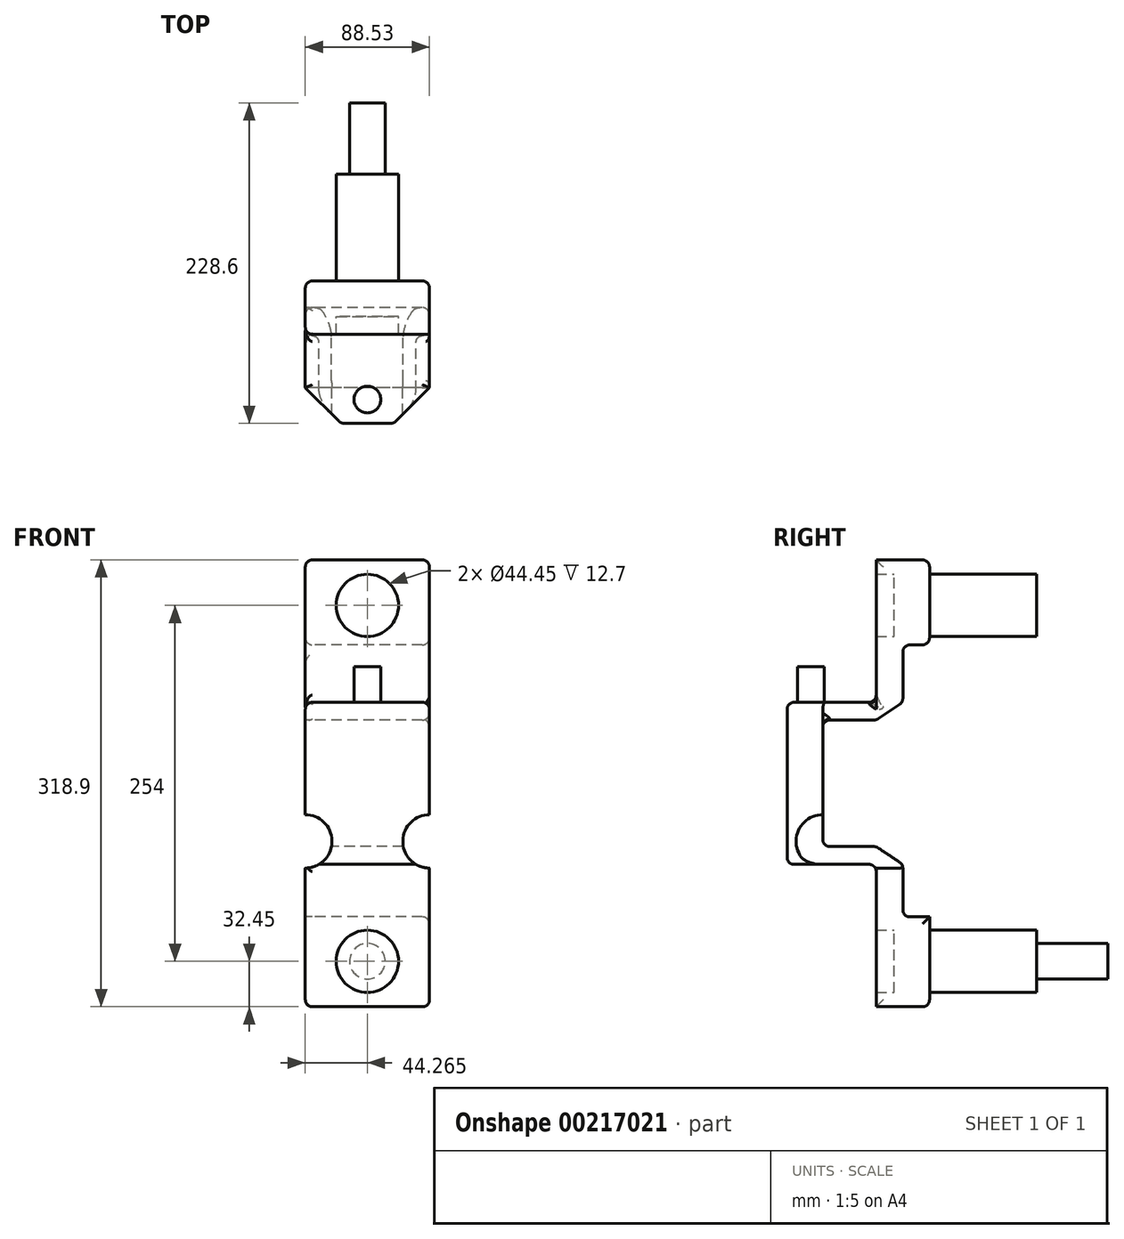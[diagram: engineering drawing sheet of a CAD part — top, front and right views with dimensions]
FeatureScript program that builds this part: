
annotation { "Feature Type Name" : "Feature", "Feature Type Description" : "" }
export const myFeature = defineFeature(function(context is Context, id is Id, definition is map)
    precondition{}
    {
        {
            var Q0;
            Q0=qCreatedBy(makeId("Front.planeOp"),FACE);
            var sketch = newSketch(context, id + "F0", { "sketchPlane" : qUnion([Q0])});
            skPoint(sketch, "E0.middle", {"position": v(-200.62, 122.45) * mm});
            skCircle(sketch, "E1", {"center": v(-200.62, 122.45) * mm, "radius": 22.23 * mm});
            skCircle(sketch, "E2", {"center": v(-200.62, -131.55) * mm, "radius": 22.23 * mm});
            skLineSegment(sketch, "E3", {"start": v(-200.62, 122.45) * mm, "end": v(-200.62, -131.55) * mm, "construction": true});
            skLineSegment(sketch, "E4.bottom", {"start": v(-156.36, -164) * mm, "end": v(-244.9, -164) * mm});
            skLineSegment(sketch, "E4.top", {"start": v(-156.36, 154.9) * mm, "end": v(-244.9, 154.9) * mm});
            skLineSegment(sketch, "E4.left", {"start": v(-156.36, -164) * mm, "end": v(-156.36, 154.9) * mm});
            skLineSegment(sketch, "E4.right", {"start": v(-244.9, -164) * mm, "end": v(-244.9, 154.9) * mm});
            skPoint(sketch, "E4.middle", {"position": v(-200.62, -4.55) * mm});
            skSolve(sketch);
        }
        {
            var Q0;
            Q0 = qSketchRegion(id + "F0", true);
            extrude(context, id + "F1", {"entities" : qUnion([Q0]), "depth" : 76.2 * mm});
        }
        {
            var Q0;
            Q0=makeQuery(id+"F1.opExtrude","SWEPT_FACE",FACE,{"disambiguationData":[OSD([sQuery(id+"F0.wireOp",EDGE,"E4.right")])]});
            var sketch = newSketch(context, id + "F2", { "sketchPlane" : qUnion([Q0])});
            skLineSegment(sketch, "E5", {"start": v(76.2, 154.9) * mm, "end": v(76.2, 53.3) * mm, "construction": true});
            skLineSegment(sketch, "E6", {"start": v(76.2, -164) * mm, "end": v(50.8, -164) * mm, "construction": true});
            skLineSegment(sketch, "E7", {"start": v(76.2, -164) * mm, "end": v(76.2, -62.4) * mm, "construction": true});
            skLineSegment(sketch, "E8", {"start": v(76.2, 154.9) * mm, "end": v(50.8, 154.9) * mm, "construction": true});
            skLineSegment(sketch, "E9", {"start": v(38.1, 154.9) * mm, "end": v(76.2, 53.3) * mm});
            skLineSegment(sketch, "E10", {"start": v(76.2, -62.4) * mm, "end": v(38.1, -164) * mm});
            skSolve(sketch);
        }
        {
            var Q0;
            {var subQ0=sQuery(id+"F2.wireOp",EDGE,"E10");Q0=makeQuery(id+"F2.imprint","IMPRINT",FACE,{"disambiguationData":[TD([[makeQuery(id+"F2.imprint","IMPRINT",EDGE,{"derivedFrom":subQ0}),1.0]])]});}
            var Q1;
            {var subQ0=sQuery(id+"F2.wireOp",EDGE,"E9");Q1=makeQuery(id+"F2.imprint","IMPRINT",FACE,{"disambiguationData":[TD([[makeQuery(id+"F2.imprint","IMPRINT",EDGE,{"derivedFrom":subQ0}),1.0]])]});}
            extrude(context, id + "F3", {"entities" : qUnion([Q0, Q1]), "operationType" : NewBodyOperationType.REMOVE, "endBound" : BoundingType.THROUGH_ALL, "oppositeDirection" : true, "depth" : 25.4 * mm});
        }
        {
            var Q0;
            Q0=makeQuery(id+"F0.imprint","IMPRINT",FACE,{"disambiguationData":[TD([[makeQuery(id+"F0.imprint","IMPRINT",EDGE,{"derivedFrom":sQuery(id+"F0.wireOp",EDGE,"E1")}),1.0]])]});
            var Q1;
            Q1=makeQuery(id+"F0.imprint","IMPRINT",FACE,{"disambiguationData":[TD([[makeQuery(id+"F0.imprint","IMPRINT",EDGE,{"derivedFrom":sQuery(id+"F0.wireOp",EDGE,"E2")}),1.0]])]});
            extrude(context, id + "F4", {"entities" : qUnion([Q0, Q1]), "operationType" : NewBodyOperationType.ADD, "depth" : 25.4 * mm, "hasSecondDirection" : true, "secondDirectionOppositeDirection" : true, "secondDirectionDepth" : 76.2 * mm});
        }
        {
            var Q0;
            Q0=makeQuery(id+"F1.opExtrude","SWEPT_FACE",FACE,{"disambiguationData":[OSD([sQuery(id+"F0.wireOp",EDGE,"E4.left")])]});
            var sketch = newSketch(context, id + "F5", { "sketchPlane" : qUnion([Q0])});
            skLineSegment(sketch, "E11", {"start": v(-38.1, 154.9) * mm, "end": v(-38.1, 53.3) * mm});
            skLineSegment(sketch, "E12", {"start": v(-38.1, 53.3) * mm, "end": v(-76.2, 53.3) * mm});
            skLineSegment(sketch, "E13", {"start": v(-76.2, -62.4) * mm, "end": v(-38.1, -62.4) * mm});
            skLineSegment(sketch, "E14", {"start": v(-38.1, -62.4) * mm, "end": v(-38.1, -164) * mm});
            skSolve(sketch);
        }
        {
            var Q0;
            Q0=makeQuery(id+"F5.imprint","IMPRINT",FACE,{"disambiguationData":[TD([[makeQuery(id+"F5.imprint","IMPRINT",EDGE,{"derivedFrom":sQuery(id+"F5.wireOp",EDGE,"E13")}),-1.0]])]});
            var Q1;
            Q1=makeQuery(id+"F5.imprint","IMPRINT",FACE,{"disambiguationData":[TD([[makeQuery(id+"F5.imprint","IMPRINT",EDGE,{"derivedFrom":sQuery(id+"F5.wireOp",EDGE,"E11")}),-1.0]])]});
            extrude(context, id + "F6", {"entities" : qUnion([Q0, Q1]), "operationType" : NewBodyOperationType.REMOVE, "endBound" : BoundingType.THROUGH_ALL, "oppositeDirection" : true, "depth" : 25.4 * mm});
        }
        {
            var Q0;
            Q0=makeQuery(id+"F4.opExtrude","CAP_FACE",FACE,{"disambiguationData":[OSD([sQuery(id+"F0.wireOp",EDGE,"E2")])],"isStart":true});
            extrude(context, id + "F7", {"entities" : qUnion([Q0]), "operationType" : NewBodyOperationType.ADD, "depth" : 50.8 * mm});
        }
        {
            var Q0;
            Q0=makeQuery(id+"F7.opExtrude","CAP_FACE",FACE,{"disambiguationData":[OSD([sQuery(id+"F0.wireOp",EDGE,"E2")])],"isStart":false});
            var sketch = newSketch(context, id + "F8", { "sketchPlane" : qUnion([Q0])});
            skCircle(sketch, "E15", {"center": v(200.62, -131.55) * mm, "radius": 12.7 * mm});
            skSolve(sketch);
        }
        {
            var Q0;
            Q0=makeQuery(id+"F8.imprint","IMPRINT",FACE,{"disambiguationData":[TD([[makeQuery(id+"F8.imprint","IMPRINT",EDGE,{"derivedFrom":sQuery(id+"F8.wireOp",EDGE,"E15")}),-1.0]])]});
            extrude(context, id + "F9", {"entities" : qUnion([Q0]), "operationType" : NewBodyOperationType.REMOVE, "oppositeDirection" : true, "depth" : 50.8 * mm});
        }
        {
            var Q0;
            Q0=makeQuery(id+"F1.opExtrude","CAP_FACE",FACE,{"disambiguationData":[OSD([sQuery(id+"F0.wireOp",EDGE,"E1"),sQuery(id+"F0.wireOp",EDGE,"E2"),sQuery(id+"F0.wireOp",EDGE,"E4.bottom"),sQuery(id+"F0.wireOp",EDGE,"E4.top"),sQuery(id+"F0.wireOp",EDGE,"E4.left"),sQuery(id+"F0.wireOp",EDGE,"E4.right")])],"isStart":false});
            extrude(context, id + "F10", {"entities" : qUnion([Q0]), "operationType" : NewBodyOperationType.ADD, "depth" : 25.4 * mm});
        }
        {
            var Q0;
            {var subQ0=sQuery(id+"F5.wireOp",EDGE,"E12");Q0=makeQuery(id+"F10.boolean.opBoolean","MERGE",FACE,{"derivedFrom":[makeQuery(id+"F6.boolean.opBoolean","COPY",FACE,{"derivedFrom":makeQuery(id+"F6.opExtrude","SWEPT_FACE",FACE,{"disambiguationData":[OSD([subQ0])]})}),makeQuery(id+"F10.opExtrude","SWEPT_FACE",FACE,{"disambiguationData":[OSD([sQuery(id+"F0.wireOp",EDGE,"E4.left"),sQuery(id+"F0.wireOp",EDGE,"E4.right"),sQuery(id+"F2.wireOp",EDGE,"E9"),subQ0])]})]});}
            var sketch = newSketch(context, id + "F11", { "sketchPlane" : qUnion([Q0])});
            skCircle(sketch, "E16", {"center": v(-200.62, -84.67) * mm, "radius": 9.53 * mm});
            skPoint(sketch, "E16.centerSnap0", {"position": v(-200.62, -101.6) * mm});
            skSolve(sketch);
        }
        {
            var Q0;
            Q0=makeQuery(id+"F11.imprint","IMPRINT",FACE,{"disambiguationData":[TD([[makeQuery(id+"F11.imprint","IMPRINT",EDGE,{"derivedFrom":sQuery(id+"F11.wireOp",EDGE,"E16")}),1.0]])]});
            extrude(context, id + "F12", {"entities" : qUnion([Q0]), "operationType" : NewBodyOperationType.ADD, "depth" : 25.4 * mm});
        }
        {
            var Q0;
            Q0=makeQuery(id+"F10.opExtrude","CAP_EDGE",EDGE,{"disambiguationData":[OSD([sQuery(id+"F0.wireOp",EDGE,"E4.right")])],"isStart":false});
            var Q1;
            Q1=makeQuery(id+"F10.opExtrude","CAP_EDGE",EDGE,{"disambiguationData":[OSD([sQuery(id+"F0.wireOp",EDGE,"E4.left")])],"isStart":false});
            chamfer(context, id + "F13", {"entities" : qUnion([Q0, Q1]), "width" : 25.4 * mm, "tangentPropagation" : true});
        }
        {
            var Q0;
            {var subQ0=sQuery(id+"F0.wireOp",EDGE,"E4.right");Q0=makeQuery(id+"F10.boolean.opBoolean","MERGE",FACE,{"derivedFrom":[makeQuery(id+"F1.opExtrude","SWEPT_FACE",FACE,{"disambiguationData":[OSD([subQ0])]}),makeQuery(id+"F10.opExtrude","SWEPT_FACE",FACE,{"disambiguationData":[OSD([subQ0])]})]});}
            var sketch = newSketch(context, id + "F14", { "sketchPlane" : qUnion([Q0])});
            skLineSegment(sketch, "E17", {"start": v(0, 94.28) * mm, "end": v(19.05, 94.28) * mm});
            skLineSegment(sketch, "E18", {"start": v(19.05, 94.28) * mm, "end": v(19.05, 53.3) * mm});
            skLineSegment(sketch, "E19", {"start": v(19.05, -99.86) * mm, "end": v(0, -99.86) * mm});
            skLineSegment(sketch, "E20.0", {"start": v(76.2, 40.6) * mm, "end": v(38.1, 40.6) * mm});
            skLineSegment(sketch, "E21.0", {"start": v(38.1, -49.7) * mm, "end": v(76.2, -49.7) * mm});
            skLineSegment(sketch, "E22", {"start": v(38.1, 40.6) * mm, "end": v(19.05, 53.3) * mm});
            skLineSegment(sketch, "E23", {"start": v(38.1, -49.7) * mm, "end": v(19.05, -62.4) * mm});
            skLineSegment(sketch, "E24.trimOffspring", {"start": v(19.05, -62.4) * mm, "end": v(19.05, -99.86) * mm});
            skSolve(sketch);
        }
        {
            var Q0;
            {var subQ2=sQuery(id+"F14.wireOp",EDGE,"E17");Q0=makeQuery(id+"F14.imprint","IMPRINT",FACE,{"disambiguationData":[TD([[makeQuery(id+"F14.imprint","IMPRINT",EDGE,{"derivedFrom":subQ2}),-1.0]])]});}
            extrude(context, id + "F15", {"entities" : qUnion([Q0]), "operationType" : NewBodyOperationType.REMOVE, "endBound" : BoundingType.THROUGH_ALL, "oppositeDirection" : true, "depth" : 25.4 * mm});
        }
        {
            var Q0;
            {var subQ0=sQuery(id+"F5.wireOp",EDGE,"E13");var subQ1=sQuery(id+"F0.wireOp",EDGE,"E4.left");Q0=makeQuery(id+"F13.opChamfer","BLEND_EDGE",EDGE,{"blendedFrom":[makeQuery(id+"F10.opExtrude","CAP_EDGE",EDGE,{"disambiguationData":[OSD([subQ1])],"isStart":false}),makeQuery(id+"F10.boolean.opBoolean","MERGE",FACE,{"derivedFrom":[makeQuery(id+"F6.boolean.opBoolean","COPY",FACE,{"derivedFrom":makeQuery(id+"F6.opExtrude","SWEPT_FACE",FACE,{"disambiguationData":[OSD([subQ0])]})}),makeQuery(id+"F10.opExtrude","SWEPT_FACE",FACE,{"disambiguationData":[OSD([subQ1,sQuery(id+"F0.wireOp",EDGE,"E4.right"),sQuery(id+"F2.wireOp",EDGE,"E10"),subQ0])]})]})],"blendedInto":[makeQuery(id+"F10.boolean.opBoolean","MERGE",FACE,{"derivedFrom":[makeQuery(id+"F6.boolean.opBoolean","COPY",FACE,{"derivedFrom":makeQuery(id+"F6.opExtrude","SWEPT_FACE",FACE,{"disambiguationData":[OSD([subQ0])]})}),makeQuery(id+"F10.opExtrude","SWEPT_FACE",FACE,{"disambiguationData":[OSD([subQ1,sQuery(id+"F0.wireOp",EDGE,"E4.right"),sQuery(id+"F2.wireOp",EDGE,"E10"),subQ0])]})]})]});}
            var Q1;
            Q1=makeQuery(id+"F10.opExtrude","CAP_EDGE",EDGE,{"disambiguationData":[OSD([sQuery(id+"F0.wireOp",EDGE,"E4.left"),sQuery(id+"F0.wireOp",EDGE,"E4.right"),sQuery(id+"F2.wireOp",EDGE,"E10"),sQuery(id+"F5.wireOp",EDGE,"E13")])],"isStart":false});
            var Q2;
            {var subQ0=sQuery(id+"F5.wireOp",EDGE,"E13");var subQ1=sQuery(id+"F0.wireOp",EDGE,"E4.right");Q2=makeQuery(id+"F13.opChamfer","BLEND_EDGE",EDGE,{"blendedFrom":[makeQuery(id+"F10.opExtrude","CAP_EDGE",EDGE,{"disambiguationData":[OSD([subQ1])],"isStart":false}),makeQuery(id+"F10.boolean.opBoolean","MERGE",FACE,{"derivedFrom":[makeQuery(id+"F6.boolean.opBoolean","COPY",FACE,{"derivedFrom":makeQuery(id+"F6.opExtrude","SWEPT_FACE",FACE,{"disambiguationData":[OSD([subQ0])]})}),makeQuery(id+"F10.opExtrude","SWEPT_FACE",FACE,{"disambiguationData":[OSD([sQuery(id+"F0.wireOp",EDGE,"E4.left"),subQ1,sQuery(id+"F2.wireOp",EDGE,"E10"),subQ0])]})]})],"blendedInto":[makeQuery(id+"F10.boolean.opBoolean","MERGE",FACE,{"derivedFrom":[makeQuery(id+"F6.boolean.opBoolean","COPY",FACE,{"derivedFrom":makeQuery(id+"F6.opExtrude","SWEPT_FACE",FACE,{"disambiguationData":[OSD([subQ0])]})}),makeQuery(id+"F10.opExtrude","SWEPT_FACE",FACE,{"disambiguationData":[OSD([sQuery(id+"F0.wireOp",EDGE,"E4.left"),subQ1,sQuery(id+"F2.wireOp",EDGE,"E10"),subQ0])]})]})]});}
            var Q3;
            {var subQ0=sQuery(id+"F0.wireOp",EDGE,"E4.right");Q3=makeQuery(id+"F10.boolean.opBoolean","MERGE",EDGE,{"derivedFrom":[makeQuery(id+"F6.boolean.opBoolean","INTERSECT",EDGE,{"derivedFrom":[makeQuery(id+"F1.opExtrude","SWEPT_FACE",FACE,{"disambiguationData":[OSD([subQ0])]}),makeQuery(id+"F6.opExtrude","SWEPT_FACE",FACE,{"disambiguationData":[OSD([sQuery(id+"F5.wireOp",EDGE,"E13")])]})]}),makeQuery(id+"F10.opExtrude","SWEPT_EDGE",EDGE,{"disambiguationData":[OSD([subQ0,sQuery(id+"F2.wireOp",EDGE,"E10")])]})]});}
            var Q4;
            Q4=makeQuery(id+"F6.boolean.opBoolean","INTERSECT",EDGE,{"derivedFrom":[makeQuery(id+"F1.opExtrude","SWEPT_FACE",FACE,{"disambiguationData":[OSD([sQuery(id+"F0.wireOp",EDGE,"E4.right")])]}),makeQuery(id+"F6.opExtrude","SWEPT_FACE",FACE,{"disambiguationData":[OSD([sQuery(id+"F5.wireOp",EDGE,"E14")])]})]});
            var Q5;
            {var subQ0=sQuery(id+"F2.wireOp",EDGE,"E10");var subQ1=sQuery(id+"F0.wireOp",EDGE,"E4.bottom");Q5=makeQuery(id+"F6.boolean.opBoolean","MERGE",EDGE,{"derivedFrom":[makeQuery(id+"F3.boolean.opBoolean","COPY",EDGE,{"derivedFrom":makeQuery(id+"F3.opExtrude","SWEPT_EDGE",EDGE,{"disambiguationData":[OSD([subQ1,sQuery(id+"F0.wireOp",EDGE,"E4.right"),subQ0])]})}),makeQuery(id+"F6.opExtrude","SWEPT_EDGE",EDGE,{"disambiguationData":[OSD([subQ1,sQuery(id+"F0.wireOp",EDGE,"E4.left"),subQ0,sQuery(id+"F5.wireOp",EDGE,"E14")])]})]});}
            var Q6;
            Q6=makeQuery(id+"F6.boolean.opBoolean","COPY",EDGE,{"derivedFrom":makeQuery(id+"F6.opExtrude","CAP_EDGE",EDGE,{"disambiguationData":[OSD([sQuery(id+"F5.wireOp",EDGE,"E14")])],"isStart":true})});
            var Q7;
            {var subQ0=sQuery(id+"F5.wireOp",EDGE,"E13");Q7=makeQuery(id+"F10.boolean.opBoolean","MERGE",EDGE,{"derivedFrom":[makeQuery(id+"F6.boolean.opBoolean","COPY",EDGE,{"derivedFrom":makeQuery(id+"F6.opExtrude","CAP_EDGE",EDGE,{"disambiguationData":[OSD([subQ0])],"isStart":true})}),makeQuery(id+"F10.opExtrude","SWEPT_EDGE",EDGE,{"disambiguationData":[OSD([sQuery(id+"F0.wireOp",EDGE,"E4.left"),sQuery(id+"F2.wireOp",EDGE,"E10"),subQ0])]})]});}
            var Q8;
            {var subQ0=sQuery(id+"F0.wireOp",EDGE,"E4.left");Q8=makeQuery(id+"F13.opChamfer","BLEND_EDGE",EDGE,{"blendedFrom":[makeQuery(id+"F10.opExtrude","CAP_EDGE",EDGE,{"disambiguationData":[OSD([subQ0])],"isStart":false}),makeQuery(id+"F10.opExtrude","CAP_FACE",FACE,{"disambiguationData":[OSD([sQuery(id+"F0.wireOp",EDGE,"E1"),sQuery(id+"F0.wireOp",EDGE,"E2"),sQuery(id+"F0.wireOp",EDGE,"E4.bottom"),sQuery(id+"F0.wireOp",EDGE,"E4.top"),subQ0,sQuery(id+"F0.wireOp",EDGE,"E4.right")])],"isStart":false})],"blendedInto":[makeQuery(id+"F10.opExtrude","CAP_FACE",FACE,{"disambiguationData":[OSD([sQuery(id+"F0.wireOp",EDGE,"E1"),sQuery(id+"F0.wireOp",EDGE,"E2"),sQuery(id+"F0.wireOp",EDGE,"E4.bottom"),sQuery(id+"F0.wireOp",EDGE,"E4.top"),subQ0,sQuery(id+"F0.wireOp",EDGE,"E4.right")])],"isStart":false})]});}
            var Q9;
            {var subQ0=sQuery(id+"F0.wireOp",EDGE,"E4.right");Q9=makeQuery(id+"F13.opChamfer","BLEND_EDGE",EDGE,{"blendedFrom":[makeQuery(id+"F10.opExtrude","CAP_EDGE",EDGE,{"disambiguationData":[OSD([subQ0])],"isStart":false}),makeQuery(id+"F10.opExtrude","CAP_FACE",FACE,{"disambiguationData":[OSD([sQuery(id+"F0.wireOp",EDGE,"E1"),sQuery(id+"F0.wireOp",EDGE,"E2"),sQuery(id+"F0.wireOp",EDGE,"E4.bottom"),sQuery(id+"F0.wireOp",EDGE,"E4.top"),sQuery(id+"F0.wireOp",EDGE,"E4.left"),subQ0])],"isStart":false})],"blendedInto":[makeQuery(id+"F10.opExtrude","CAP_FACE",FACE,{"disambiguationData":[OSD([sQuery(id+"F0.wireOp",EDGE,"E1"),sQuery(id+"F0.wireOp",EDGE,"E2"),sQuery(id+"F0.wireOp",EDGE,"E4.bottom"),sQuery(id+"F0.wireOp",EDGE,"E4.top"),sQuery(id+"F0.wireOp",EDGE,"E4.left"),subQ0])],"isStart":false})]});}
            var Q10;
            {var subQ0=sQuery(id+"F5.wireOp",EDGE,"E12");var subQ1=sQuery(id+"F0.wireOp",EDGE,"E4.left");Q10=makeQuery(id+"F13.opChamfer","BLEND_EDGE",EDGE,{"blendedFrom":[makeQuery(id+"F10.opExtrude","CAP_EDGE",EDGE,{"disambiguationData":[OSD([subQ1])],"isStart":false}),makeQuery(id+"F10.boolean.opBoolean","MERGE",FACE,{"derivedFrom":[makeQuery(id+"F6.boolean.opBoolean","COPY",FACE,{"derivedFrom":makeQuery(id+"F6.opExtrude","SWEPT_FACE",FACE,{"disambiguationData":[OSD([subQ0])]})}),makeQuery(id+"F10.opExtrude","SWEPT_FACE",FACE,{"disambiguationData":[OSD([subQ1,sQuery(id+"F0.wireOp",EDGE,"E4.right"),sQuery(id+"F2.wireOp",EDGE,"E9"),subQ0])]})]})],"blendedInto":[makeQuery(id+"F10.boolean.opBoolean","MERGE",FACE,{"derivedFrom":[makeQuery(id+"F6.boolean.opBoolean","COPY",FACE,{"derivedFrom":makeQuery(id+"F6.opExtrude","SWEPT_FACE",FACE,{"disambiguationData":[OSD([subQ0])]})}),makeQuery(id+"F10.opExtrude","SWEPT_FACE",FACE,{"disambiguationData":[OSD([subQ1,sQuery(id+"F0.wireOp",EDGE,"E4.right"),sQuery(id+"F2.wireOp",EDGE,"E9"),subQ0])]})]})]});}
            var Q11;
            Q11=makeQuery(id+"F10.opExtrude","CAP_EDGE",EDGE,{"disambiguationData":[OSD([sQuery(id+"F0.wireOp",EDGE,"E4.left"),sQuery(id+"F0.wireOp",EDGE,"E4.right"),sQuery(id+"F2.wireOp",EDGE,"E9"),sQuery(id+"F5.wireOp",EDGE,"E12")])],"isStart":false});
            var Q12;
            {var subQ0=sQuery(id+"F5.wireOp",EDGE,"E12");var subQ1=sQuery(id+"F0.wireOp",EDGE,"E4.right");Q12=makeQuery(id+"F13.opChamfer","BLEND_EDGE",EDGE,{"blendedFrom":[makeQuery(id+"F10.opExtrude","CAP_EDGE",EDGE,{"disambiguationData":[OSD([subQ1])],"isStart":false}),makeQuery(id+"F10.boolean.opBoolean","MERGE",FACE,{"derivedFrom":[makeQuery(id+"F6.boolean.opBoolean","COPY",FACE,{"derivedFrom":makeQuery(id+"F6.opExtrude","SWEPT_FACE",FACE,{"disambiguationData":[OSD([subQ0])]})}),makeQuery(id+"F10.opExtrude","SWEPT_FACE",FACE,{"disambiguationData":[OSD([sQuery(id+"F0.wireOp",EDGE,"E4.left"),subQ1,sQuery(id+"F2.wireOp",EDGE,"E9"),subQ0])]})]})],"blendedInto":[makeQuery(id+"F10.boolean.opBoolean","MERGE",FACE,{"derivedFrom":[makeQuery(id+"F6.boolean.opBoolean","COPY",FACE,{"derivedFrom":makeQuery(id+"F6.opExtrude","SWEPT_FACE",FACE,{"disambiguationData":[OSD([subQ0])]})}),makeQuery(id+"F10.opExtrude","SWEPT_FACE",FACE,{"disambiguationData":[OSD([sQuery(id+"F0.wireOp",EDGE,"E4.left"),subQ1,sQuery(id+"F2.wireOp",EDGE,"E9"),subQ0])]})]})]});}
            var Q13;
            Q13=makeQuery(id+"F6.boolean.opBoolean","INTERSECT",EDGE,{"derivedFrom":[makeQuery(id+"F1.opExtrude","SWEPT_FACE",FACE,{"disambiguationData":[OSD([sQuery(id+"F0.wireOp",EDGE,"E4.right")])]}),makeQuery(id+"F6.opExtrude","SWEPT_FACE",FACE,{"disambiguationData":[OSD([sQuery(id+"F5.wireOp",EDGE,"E11")])]})]});
            var Q14;
            {var subQ0=sQuery(id+"F2.wireOp",EDGE,"E9");var subQ1=sQuery(id+"F0.wireOp",EDGE,"E4.top");Q14=makeQuery(id+"F6.boolean.opBoolean","MERGE",EDGE,{"derivedFrom":[makeQuery(id+"F3.boolean.opBoolean","COPY",EDGE,{"derivedFrom":makeQuery(id+"F3.opExtrude","SWEPT_EDGE",EDGE,{"disambiguationData":[OSD([subQ1,sQuery(id+"F0.wireOp",EDGE,"E4.right"),subQ0])]})}),makeQuery(id+"F6.opExtrude","SWEPT_EDGE",EDGE,{"disambiguationData":[OSD([subQ1,sQuery(id+"F0.wireOp",EDGE,"E4.left"),subQ0,sQuery(id+"F5.wireOp",EDGE,"E11")])]})]});}
            var Q15;
            Q15=makeQuery(id+"F6.boolean.opBoolean","COPY",EDGE,{"derivedFrom":makeQuery(id+"F6.opExtrude","CAP_EDGE",EDGE,{"disambiguationData":[OSD([sQuery(id+"F5.wireOp",EDGE,"E11")])],"isStart":true})});
            var Q16;
            Q16=makeQuery(id+"F1.opExtrude","SWEPT_EDGE",EDGE,{"disambiguationData":[OSD([sQuery(id+"F0.wireOp",EDGE,"E4.top"),sQuery(id+"F0.wireOp",EDGE,"E4.left")])]});
            var Q17;
            {var subQ0=sQuery(id+"F0.wireOp",EDGE,"E4.left");var subQ1=sQuery(id+"F0.wireOp",EDGE,"E4.top");Q17=makeQuery(id+"F15.boolean.opBoolean","SPLIT",EDGE,{"disambiguationData":[TD([makeQuery(id+"F1.opExtrude","SWEPT_FACE",FACE,{"disambiguationData":[OSD([subQ1])]})])],"derivedFrom":makeQuery(id+"F1.opExtrude","CAP_EDGE",EDGE,{"disambiguationData":[OSD([subQ0])],"isStart":true})});}
            var Q18;
            {var subQ0=sQuery(id+"F0.wireOp",EDGE,"E4.left");Q18=makeQuery(id+"F15.boolean.opBoolean","INTERSECT",EDGE,{"derivedFrom":[makeQuery(id+"F10.boolean.opBoolean","MERGE",FACE,{"derivedFrom":[makeQuery(id+"F1.opExtrude","SWEPT_FACE",FACE,{"disambiguationData":[OSD([subQ0])]}),makeQuery(id+"F10.opExtrude","SWEPT_FACE",FACE,{"disambiguationData":[OSD([subQ0])]})]}),makeQuery(id+"F15.opExtrude","SWEPT_FACE",FACE,{"disambiguationData":[OSD([sQuery(id+"F14.wireOp",EDGE,"E21.0")])]})]});}
            var Q19;
            {var subQ0=sQuery(id+"F0.wireOp",EDGE,"E4.left");Q19=makeQuery(id+"F15.boolean.opBoolean","INTERSECT",EDGE,{"derivedFrom":[makeQuery(id+"F10.boolean.opBoolean","MERGE",FACE,{"derivedFrom":[makeQuery(id+"F1.opExtrude","SWEPT_FACE",FACE,{"disambiguationData":[OSD([subQ0])]}),makeQuery(id+"F10.opExtrude","SWEPT_FACE",FACE,{"disambiguationData":[OSD([subQ0])]})]}),makeQuery(id+"F15.opExtrude","SWEPT_FACE",FACE,{"disambiguationData":[OSD([sQuery(id+"F14.wireOp",EDGE,"E23")])]})]});}
            var Q20;
            {var subQ0=sQuery(id+"F0.wireOp",EDGE,"E4.left");Q20=makeQuery(id+"F15.boolean.opBoolean","INTERSECT",EDGE,{"derivedFrom":[makeQuery(id+"F10.boolean.opBoolean","MERGE",FACE,{"derivedFrom":[makeQuery(id+"F1.opExtrude","SWEPT_FACE",FACE,{"disambiguationData":[OSD([subQ0])]}),makeQuery(id+"F10.opExtrude","SWEPT_FACE",FACE,{"disambiguationData":[OSD([subQ0])]})]}),makeQuery(id+"F15.opExtrude","SWEPT_FACE",FACE,{"disambiguationData":[OSD([sQuery(id+"F14.wireOp",EDGE,"E24.trimOffspring")])]})]});}
            var Q21;
            {var subQ0=sQuery(id+"F0.wireOp",EDGE,"E4.left");Q21=makeQuery(id+"F15.boolean.opBoolean","INTERSECT",EDGE,{"derivedFrom":[makeQuery(id+"F10.boolean.opBoolean","MERGE",FACE,{"derivedFrom":[makeQuery(id+"F1.opExtrude","SWEPT_FACE",FACE,{"disambiguationData":[OSD([subQ0])]}),makeQuery(id+"F10.opExtrude","SWEPT_FACE",FACE,{"disambiguationData":[OSD([subQ0])]})]}),makeQuery(id+"F15.opExtrude","SWEPT_FACE",FACE,{"disambiguationData":[OSD([sQuery(id+"F14.wireOp",EDGE,"E19")])]})]});}
            var Q22;
            {var subQ0=sQuery(id+"F0.wireOp",EDGE,"E4.left");var subQ1=sQuery(id+"F0.wireOp",EDGE,"E4.bottom");Q22=makeQuery(id+"F15.boolean.opBoolean","SPLIT",EDGE,{"disambiguationData":[TD([makeQuery(id+"F1.opExtrude","SWEPT_FACE",FACE,{"disambiguationData":[OSD([subQ1])]})])],"derivedFrom":makeQuery(id+"F1.opExtrude","CAP_EDGE",EDGE,{"disambiguationData":[OSD([subQ0])],"isStart":true})});}
            var Q23;
            Q23=makeQuery(id+"F1.opExtrude","SWEPT_EDGE",EDGE,{"disambiguationData":[OSD([sQuery(id+"F0.wireOp",EDGE,"E4.bottom"),sQuery(id+"F0.wireOp",EDGE,"E4.left")])]});
            var Q24;
            Q24=makeQuery(id+"F1.opExtrude","CAP_EDGE",EDGE,{"disambiguationData":[OSD([sQuery(id+"F0.wireOp",EDGE,"E4.bottom")])],"isStart":true});
            var Q25;
            Q25=makeQuery(id+"F1.opExtrude","SWEPT_EDGE",EDGE,{"disambiguationData":[OSD([sQuery(id+"F0.wireOp",EDGE,"E4.bottom"),sQuery(id+"F0.wireOp",EDGE,"E4.right")])]});
            var Q26;
            {var subQ0=sQuery(id+"F0.wireOp",EDGE,"E4.right");var subQ1=sQuery(id+"F0.wireOp",EDGE,"E4.bottom");Q26=makeQuery(id+"F15.boolean.opBoolean","SPLIT",EDGE,{"disambiguationData":[TD([makeQuery(id+"F1.opExtrude","SWEPT_FACE",FACE,{"disambiguationData":[OSD([subQ1])]})])],"derivedFrom":makeQuery(id+"F1.opExtrude","CAP_EDGE",EDGE,{"disambiguationData":[OSD([subQ0])],"isStart":true})});}
            var Q27;
            Q27=makeQuery(id+"F15.boolean.opBoolean","COPY",EDGE,{"derivedFrom":makeQuery(id+"F15.opExtrude","CAP_EDGE",EDGE,{"disambiguationData":[OSD([sQuery(id+"F14.wireOp",EDGE,"E19")])],"isStart":true})});
            var Q28;
            Q28=makeQuery(id+"F15.boolean.opBoolean","COPY",EDGE,{"derivedFrom":makeQuery(id+"F15.opExtrude","CAP_EDGE",EDGE,{"disambiguationData":[OSD([sQuery(id+"F14.wireOp",EDGE,"E24.trimOffspring")])],"isStart":true})});
            var Q29;
            Q29=makeQuery(id+"F15.boolean.opBoolean","COPY",EDGE,{"derivedFrom":makeQuery(id+"F15.opExtrude","CAP_EDGE",EDGE,{"disambiguationData":[OSD([sQuery(id+"F14.wireOp",EDGE,"E23")])],"isStart":true})});
            var Q30;
            Q30=makeQuery(id+"F15.boolean.opBoolean","COPY",EDGE,{"derivedFrom":makeQuery(id+"F15.opExtrude","CAP_EDGE",EDGE,{"disambiguationData":[OSD([sQuery(id+"F14.wireOp",EDGE,"E21.0")])],"isStart":true})});
            var Q31;
            Q31=makeQuery(id+"F15.boolean.opBoolean","COPY",EDGE,{"derivedFrom":makeQuery(id+"F15.opExtrude","CAP_EDGE",EDGE,{"disambiguationData":[OSD([sQuery(id+"F14.wireOp",EDGE,"E20.0")])],"isStart":true})});
            var Q32;
            Q32=makeQuery(id+"F15.boolean.opBoolean","COPY",EDGE,{"derivedFrom":makeQuery(id+"F15.opExtrude","CAP_EDGE",EDGE,{"disambiguationData":[OSD([sQuery(id+"F14.wireOp",EDGE,"E22")])],"isStart":true})});
            var Q33;
            Q33=makeQuery(id+"F15.boolean.opBoolean","COPY",EDGE,{"derivedFrom":makeQuery(id+"F15.opExtrude","CAP_EDGE",EDGE,{"disambiguationData":[OSD([sQuery(id+"F14.wireOp",EDGE,"E18")])],"isStart":true})});
            var Q34;
            Q34=makeQuery(id+"F15.boolean.opBoolean","COPY",EDGE,{"derivedFrom":makeQuery(id+"F15.opExtrude","CAP_EDGE",EDGE,{"disambiguationData":[OSD([sQuery(id+"F14.wireOp",EDGE,"E17")])],"isStart":true})});
            var Q35;
            {var subQ0=sQuery(id+"F0.wireOp",EDGE,"E4.right");var subQ1=sQuery(id+"F0.wireOp",EDGE,"E4.top");Q35=makeQuery(id+"F15.boolean.opBoolean","SPLIT",EDGE,{"disambiguationData":[TD([makeQuery(id+"F1.opExtrude","SWEPT_FACE",FACE,{"disambiguationData":[OSD([subQ1])]})])],"derivedFrom":makeQuery(id+"F1.opExtrude","CAP_EDGE",EDGE,{"disambiguationData":[OSD([subQ0])],"isStart":true})});}
            var Q36;
            Q36=makeQuery(id+"F1.opExtrude","SWEPT_EDGE",EDGE,{"disambiguationData":[OSD([sQuery(id+"F0.wireOp",EDGE,"E4.top"),sQuery(id+"F0.wireOp",EDGE,"E4.right")])]});
            var Q37;
            Q37=makeQuery(id+"F1.opExtrude","CAP_EDGE",EDGE,{"disambiguationData":[OSD([sQuery(id+"F0.wireOp",EDGE,"E4.top")])],"isStart":true});
            var Q38;
            {var subQ0=sQuery(id+"F5.wireOp",EDGE,"E12");Q38=makeQuery(id+"F10.boolean.opBoolean","MERGE",EDGE,{"derivedFrom":[makeQuery(id+"F6.boolean.opBoolean","COPY",EDGE,{"derivedFrom":makeQuery(id+"F6.opExtrude","CAP_EDGE",EDGE,{"disambiguationData":[OSD([subQ0])],"isStart":true})}),makeQuery(id+"F10.opExtrude","SWEPT_EDGE",EDGE,{"disambiguationData":[OSD([sQuery(id+"F0.wireOp",EDGE,"E4.left"),sQuery(id+"F2.wireOp",EDGE,"E9"),subQ0])]})]});}
            var Q39;
            {var subQ0=sQuery(id+"F0.wireOp",EDGE,"E4.right");Q39=makeQuery(id+"F10.boolean.opBoolean","MERGE",EDGE,{"derivedFrom":[makeQuery(id+"F6.boolean.opBoolean","INTERSECT",EDGE,{"derivedFrom":[makeQuery(id+"F1.opExtrude","SWEPT_FACE",FACE,{"disambiguationData":[OSD([subQ0])]}),makeQuery(id+"F6.opExtrude","SWEPT_FACE",FACE,{"disambiguationData":[OSD([sQuery(id+"F5.wireOp",EDGE,"E12")])]})]}),makeQuery(id+"F10.opExtrude","SWEPT_EDGE",EDGE,{"disambiguationData":[OSD([subQ0,sQuery(id+"F2.wireOp",EDGE,"E9")])]})]});}
            var Q40;
            Q40=makeQuery(id+"F15.boolean.opBoolean","COPY",EDGE,{"derivedFrom":makeQuery(id+"F15.opExtrude","SWEPT_EDGE",EDGE,{"disambiguationData":[OSD([sQuery(id+"F0.wireOp",EDGE,"E4.right"),sQuery(id+"F14.wireOp",EDGE,"E19")])]})});
            var Q41;
            Q41=makeQuery(id+"F15.boolean.opBoolean","COPY",EDGE,{"derivedFrom":makeQuery(id+"F15.opExtrude","SWEPT_EDGE",EDGE,{"disambiguationData":[OSD([sQuery(id+"F14.wireOp",EDGE,"E19"),sQuery(id+"F14.wireOp",EDGE,"E24.trimOffspring")])]})});
            var Q42;
            Q42=makeQuery(id+"F15.boolean.opBoolean","COPY",EDGE,{"derivedFrom":makeQuery(id+"F15.opExtrude","SWEPT_EDGE",EDGE,{"disambiguationData":[OSD([sQuery(id+"F14.wireOp",EDGE,"E23"),sQuery(id+"F14.wireOp",EDGE,"E24.trimOffspring")])]})});
            var Q43;
            Q43=makeQuery(id+"F15.boolean.opBoolean","COPY",EDGE,{"derivedFrom":makeQuery(id+"F15.opExtrude","SWEPT_EDGE",EDGE,{"disambiguationData":[OSD([sQuery(id+"F14.wireOp",EDGE,"E21.0"),sQuery(id+"F14.wireOp",EDGE,"E23")])]})});
            fillet(context, id + "F16", {"entities" : qUnion([Q0, Q1, Q2, Q3, Q4, Q5, Q6, Q7, Q8, Q9, Q10, Q11, Q12, Q13, Q14, Q15, Q16, Q17, Q18, Q19, Q20, Q21, Q22, Q23, Q24, Q25, Q26, Q27, Q28, Q29, Q30, Q31, Q32, Q33, Q34, Q35, Q36, Q37, Q38, Q39, Q40, Q41, Q42, Q43]), "radius" : 5.08 * mm, "tangentPropagation" : true, "allowEdgeOverflow" : false});
        }
        {
            var Q0;
            {var subQ0=sQuery(id+"F0.wireOp",EDGE,"E4.left");Q0=makeQuery(id+"F15.boolean.opBoolean","INTERSECT",EDGE,{"derivedFrom":[makeQuery(id+"F10.boolean.opBoolean","MERGE",FACE,{"derivedFrom":[makeQuery(id+"F1.opExtrude","SWEPT_FACE",FACE,{"disambiguationData":[OSD([subQ0])]}),makeQuery(id+"F10.opExtrude","SWEPT_FACE",FACE,{"disambiguationData":[OSD([subQ0])]})]}),makeQuery(id+"F15.opExtrude","SWEPT_FACE",FACE,{"disambiguationData":[OSD([sQuery(id+"F14.wireOp",EDGE,"E20.0")])]})]});}
            var Q1;
            Q1=makeQuery(id+"F15.boolean.opBoolean","COPY",FACE,{"derivedFrom":makeQuery(id+"F15.opExtrude","SWEPT_FACE",FACE,{"disambiguationData":[OSD([sQuery(id+"F14.wireOp",EDGE,"E22")])]})});
            var Q2;
            {var subQ0=sQuery(id+"F0.wireOp",EDGE,"E4.left");Q2=makeQuery(id+"F15.boolean.opBoolean","INTERSECT",EDGE,{"derivedFrom":[makeQuery(id+"F10.boolean.opBoolean","MERGE",FACE,{"derivedFrom":[makeQuery(id+"F1.opExtrude","SWEPT_FACE",FACE,{"disambiguationData":[OSD([subQ0])]}),makeQuery(id+"F10.opExtrude","SWEPT_FACE",FACE,{"disambiguationData":[OSD([subQ0])]})]}),makeQuery(id+"F15.opExtrude","SWEPT_FACE",FACE,{"disambiguationData":[OSD([sQuery(id+"F14.wireOp",EDGE,"E17")])]})]});}
            var Q3;
            {var subQ0=sQuery(id+"F0.wireOp",EDGE,"E4.left");Q3=makeQuery(id+"F15.boolean.opBoolean","INTERSECT",EDGE,{"derivedFrom":[makeQuery(id+"F10.boolean.opBoolean","MERGE",FACE,{"derivedFrom":[makeQuery(id+"F1.opExtrude","SWEPT_FACE",FACE,{"disambiguationData":[OSD([subQ0])]}),makeQuery(id+"F10.opExtrude","SWEPT_FACE",FACE,{"disambiguationData":[OSD([subQ0])]})]}),makeQuery(id+"F15.opExtrude","SWEPT_FACE",FACE,{"disambiguationData":[OSD([sQuery(id+"F14.wireOp",EDGE,"E18")])]})]});}
            var Q4;
            Q4=makeQuery(id+"F15.boolean.opBoolean","COPY",EDGE,{"derivedFrom":makeQuery(id+"F15.opExtrude","SWEPT_EDGE",EDGE,{"disambiguationData":[OSD([sQuery(id+"F14.wireOp",EDGE,"E17"),sQuery(id+"F14.wireOp",EDGE,"E18")])]})});
            fillet(context, id + "F17", {"entities" : qUnion([Q0, Q1, Q2, Q3, Q4]), "radius" : 5.08 * mm, "tangentPropagation" : true, "allowEdgeOverflow" : false});
        }
        {
            var Q0;
            Q0=makeQuery(id+"F6.boolean.opBoolean","COPY",EDGE,{"derivedFrom":makeQuery(id+"F6.opExtrude","SWEPT_EDGE",EDGE,{"disambiguationData":[OSD([sQuery(id+"F5.wireOp",EDGE,"E11"),sQuery(id+"F5.wireOp",EDGE,"E12")])]})});
            var Q1;
            Q1=makeQuery(id+"F6.boolean.opBoolean","COPY",EDGE,{"derivedFrom":makeQuery(id+"F6.opExtrude","SWEPT_EDGE",EDGE,{"disambiguationData":[OSD([sQuery(id+"F5.wireOp",EDGE,"E13"),sQuery(id+"F5.wireOp",EDGE,"E14")])]})});
            fillet(context, id + "F18", {"entities" : qUnion([Q0, Q1]), "radius" : 5.08 * mm, "tangentPropagation" : true, "allowEdgeOverflow" : false});
        }
        {
            var Q0;
            Q0=makeQuery(id+"F15.boolean.opBoolean","COPY",EDGE,{"derivedFrom":makeQuery(id+"F15.opExtrude","SWEPT_EDGE",EDGE,{"disambiguationData":[OSD([sQuery(id+"F0.wireOp",EDGE,"E4.right"),sQuery(id+"F14.wireOp",EDGE,"E20.0")])]})});
            var Q1;
            Q1=makeQuery(id+"F15.boolean.opBoolean","COPY",EDGE,{"derivedFrom":makeQuery(id+"F15.opExtrude","SWEPT_EDGE",EDGE,{"disambiguationData":[OSD([sQuery(id+"F0.wireOp",EDGE,"E4.right"),sQuery(id+"F14.wireOp",EDGE,"E21.0")])]})});
            fillet(context, id + "F19", {"entities" : qUnion([Q0, Q1]), "radius" : 5.08 * mm, "tangentPropagation" : true, "allowEdgeOverflow" : false});
        }
        {
            var Q0;
            {var subQ0=sQuery(id+"F0.wireOp",EDGE,"E4.right");var subQ1=makeQuery(id+"F13.opChamfer","BLEND_EDGE",EDGE,{"blendedFrom":[makeQuery(id+"F10.opExtrude","CAP_EDGE",EDGE,{"disambiguationData":[OSD([subQ0])],"isStart":false}),makeQuery(id+"F10.boolean.opBoolean","MERGE",FACE,{"derivedFrom":[makeQuery(id+"F1.opExtrude","SWEPT_FACE",FACE,{"disambiguationData":[OSD([subQ0])]}),makeQuery(id+"F10.opExtrude","SWEPT_FACE",FACE,{"disambiguationData":[OSD([subQ0])]})]})],"blendedInto":[makeQuery(id+"F10.boolean.opBoolean","MERGE",FACE,{"derivedFrom":[makeQuery(id+"F1.opExtrude","SWEPT_FACE",FACE,{"disambiguationData":[OSD([subQ0])]}),makeQuery(id+"F10.opExtrude","SWEPT_FACE",FACE,{"disambiguationData":[OSD([subQ0])]})]})]});Q0=makeQuery(id+"F15.boolean.opBoolean","COPY",FACE,{"derivedFrom":makeQuery(id+"F15.opExtrude","SWEPT_FACE",FACE,{"disambiguationData":[OSD([subQ0]),TDD([makeQuery(id+"F14.imprint","IMPRINT",EDGE,{"disambiguationData":[TD([[makeQuery(id+"F14.imprint","INTERSECT",VERTEX,{"derivedFrom":[subQ1,sQuery(id+"F14.wireOp",EDGE,"E20.0")]}),1.0]])],"derivedFrom":subQ1})])]})});}
            var sketch = newSketch(context, id + "F20", { "sketchPlane" : qUnion([Q0])});
            skCircle(sketch, "E25", {"center": v(156.36, -45.98) * mm, "radius": 19.05 * mm});
            skCircle(sketch, "E26", {"center": v(244.9, -45.98) * mm, "radius": 19.05 * mm});
            skSolve(sketch);
        }
        {
            var Q0;
            Q0 = qSketchRegion(id + "F20", true);
            extrude(context, id + "F21", {"entities" : qUnion([Q0]), "operationType" : NewBodyOperationType.REMOVE, "endBound" : BoundingType.THROUGH_ALL, "oppositeDirection" : true, "depth" : 25.4 * mm, "hasSecondDirection" : true, "secondDirectionBound" : BoundingType.THROUGH_ALL, "secondDirectionOppositeDirection" : false, "secondDirectionDepth" : 25.4 * mm});
        }
    });
